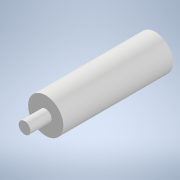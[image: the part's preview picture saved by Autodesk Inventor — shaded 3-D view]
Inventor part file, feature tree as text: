
AUTODESK INVENTOR PART (.ipt)
format: ipt  version: 2022.3 (Build 263350000, 350)  size: 99,328 bytes
history: native  units: mm
features: extrude x2, sketch x2
ambient origin geometry x8: Origin, YZ Plane, XZ Plane, XY Plane, X Axis, Y Axis, Z Axis, Center Point
bodies: Solid1 (feature_tree)
feature tree (4):
  extrude  "Extrusion1"  Depth=18.7mm TaperAngle=0.0deg
  extrude  "Extrusion2"  Depth=3.6mm TaperAngle=0.0deg
  sketch  "Sketch1"  dims[d0=6.0mm d1=18.7mm d2=0.0mm]
  sketch  "Sketch2"  dims[d3=2.0mm d4=3.6mm d5=0.0mm]
